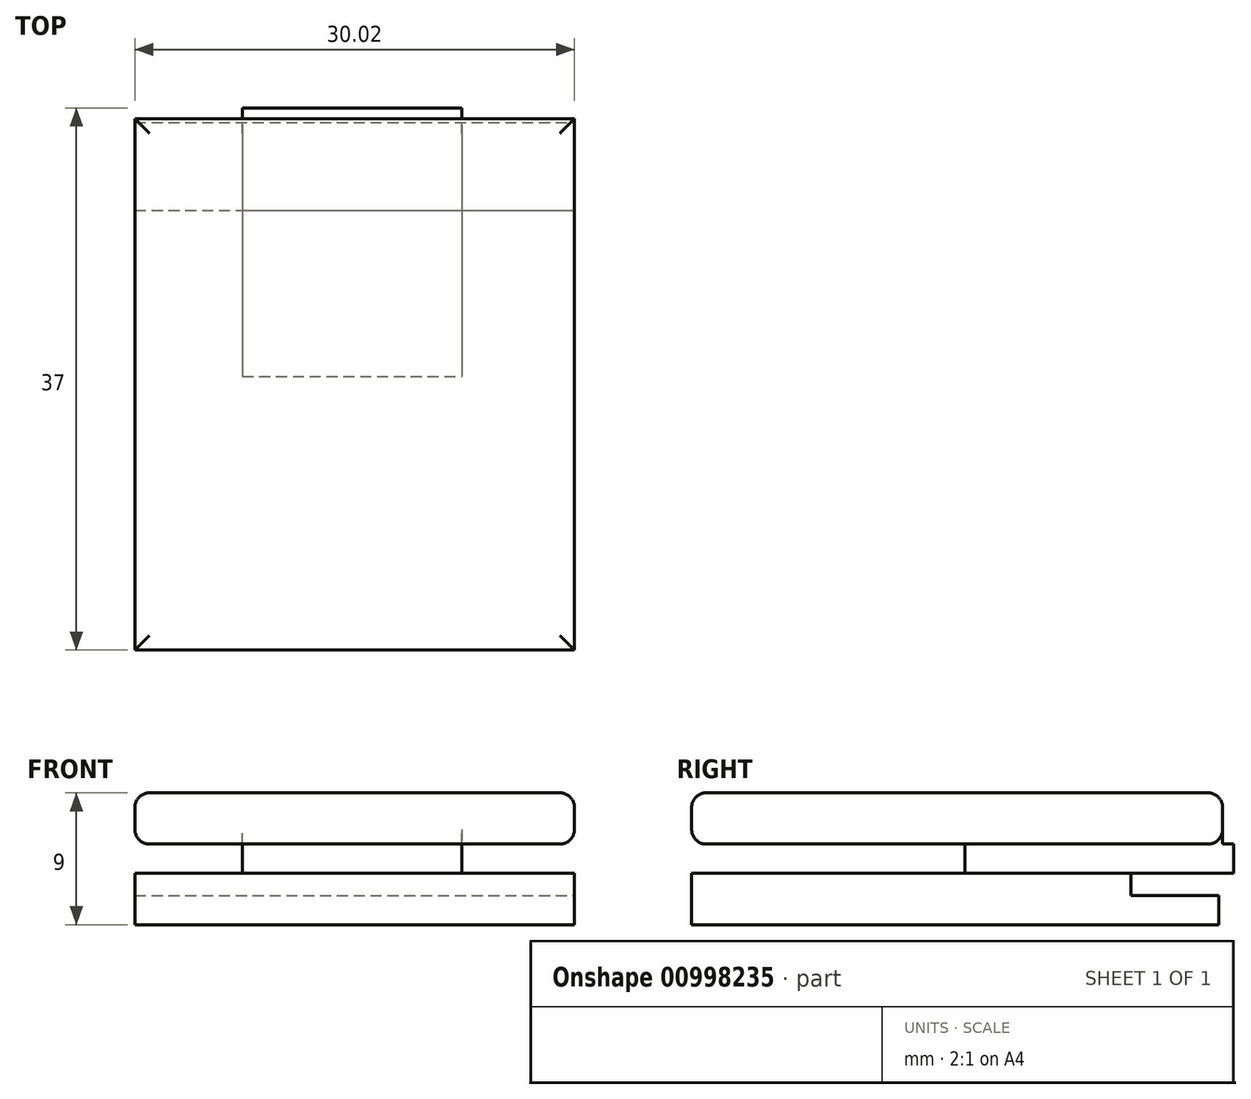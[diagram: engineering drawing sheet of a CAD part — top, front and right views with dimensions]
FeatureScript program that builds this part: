
annotation { "Feature Type Name" : "Feature", "Feature Type Description" : "" }
export const myFeature = defineFeature(function(context is Context, id is Id, definition is map)
    precondition{}
    {
        {
            var Q0;
            Q0=qCreatedBy(makeId("Top.planeOp"),FACE);
            var sketch = newSketch(context, id + "F0", { "sketchPlane" : qUnion([Q0])});
            skLineSegment(sketch, "E0.bottom", {"start": v(0, 0) * mm, "end": v(30, 0) * mm});
            skLineSegment(sketch, "E0.top", {"start": v(0, 30) * mm, "end": v(30, 30) * mm});
            skLineSegment(sketch, "E0.left", {"start": v(0, 0) * mm, "end": v(0, 30) * mm});
            skLineSegment(sketch, "E0.right", {"start": v(30, 0) * mm, "end": v(30, 30) * mm});
            skSolve(sketch);
        }
        {
            var Q0;
            Q0=makeQuery(id+"F0.imprint","IMPRINT",FACE,{"disambiguationData":[TD([[makeQuery(id+"F0.imprint","IMPRINT",EDGE,{"derivedFrom":sQuery(id+"F0.wireOp",EDGE,"E0.bottom")}),1.0]])]});
            extrude(context, id + "F1", {"entities" : qUnion([Q0]), "depth" : 1.5 * mm, "offsetDistance" : 25 * mm});
        }
        {
            var Q0;
            Q0=makeQuery(id+"F1.opExtrude","CAP_FACE",FACE,{"disambiguationData":[OSD([sQuery(id+"F0.wireOp",EDGE,"E0.bottom"),sQuery(id+"F0.wireOp",EDGE,"E0.top"),sQuery(id+"F0.wireOp",EDGE,"E0.left"),sQuery(id+"F0.wireOp",EDGE,"E0.right")])],"isStart":false});
            var sketch = newSketch(context, id + "F2", { "sketchPlane" : qUnion([Q0])});
            skLineSegment(sketch, "E1.bottom", {"start": v(7.34, 37) * mm, "end": v(22.34, 37) * mm});
            skLineSegment(sketch, "E1.top", {"start": v(7.34, 18.66) * mm, "end": v(22.34, 18.66) * mm});
            skLineSegment(sketch, "E1.left", {"start": v(7.34, 37) * mm, "end": v(7.34, 18.66) * mm});
            skLineSegment(sketch, "E1.right", {"start": v(22.34, 37) * mm, "end": v(22.34, 18.66) * mm});
            skSolve(sketch);
        }
        {
            var Q0;
            Q0 = qSketchRegion(id + "F2", true);
            extrude(context, id + "F3", {"entities" : qUnion([Q0]), "operationType" : NewBodyOperationType.ADD, "depth" : 2 * mm, "offsetDistance" : 25 * mm});
        }
        {
            var Q0;
            Q0=makeQuery(id+"F1.opExtrude","CAP_FACE",FACE,{"disambiguationData":[OSD([sQuery(id+"F0.wireOp",EDGE,"E0.bottom"),sQuery(id+"F0.wireOp",EDGE,"E0.top"),sQuery(id+"F0.wireOp",EDGE,"E0.left"),sQuery(id+"F0.wireOp",EDGE,"E0.right")])],"isStart":true});
            var sketch = newSketch(context, id + "F4", { "sketchPlane" : qUnion([Q0])});
            skLineSegment(sketch, "E2.bottom", {"start": v(0, 0) * mm, "end": v(30, 0) * mm});
            skLineSegment(sketch, "E2.top", {"start": v(0, -36) * mm, "end": v(30, -36) * mm});
            skLineSegment(sketch, "E2.left", {"start": v(0, 0) * mm, "end": v(0, -36) * mm});
            skLineSegment(sketch, "E2.right", {"start": v(30, 0) * mm, "end": v(30, -36) * mm});
            skSolve(sketch);
        }
        {
            var Q0;
            Q0 = qSketchRegion(id + "F4", true);
            extrude(context, id + "F5", {"entities" : qUnion([Q0]), "operationType" : NewBodyOperationType.ADD, "depth" : 2 * mm, "offsetDistance" : 25 * mm});
        }
        {
            var Q0;
            Q0=makeQuery(id+"F3.opExtrude","CAP_FACE",FACE,{"disambiguationData":[OSD([sQuery(id+"F2.wireOp",EDGE,"E1.bottom"),sQuery(id+"F2.wireOp",EDGE,"E1.top"),sQuery(id+"F2.wireOp",EDGE,"E1.left"),sQuery(id+"F2.wireOp",EDGE,"E1.right")])],"isStart":false});
            var sketch = newSketch(context, id + "F6", { "sketchPlane" : qUnion([Q0])});
            skLineSegment(sketch, "E3.bottom", {"start": v(0, 0) * mm, "end": v(30.02, 0) * mm});
            skLineSegment(sketch, "E3.top", {"start": v(0, 36.26) * mm, "end": v(30.02, 36.26) * mm});
            skLineSegment(sketch, "E3.left", {"start": v(0, 0) * mm, "end": v(0, 36.26) * mm});
            skLineSegment(sketch, "E3.right", {"start": v(30.02, 0) * mm, "end": v(30.02, 36.26) * mm});
            skSolve(sketch);
        }
        {
            var Q0;
            Q0 = qSketchRegion(id + "F6", true);
            extrude(context, id + "F7", {"entities" : qUnion([Q0]), "operationType" : NewBodyOperationType.ADD, "depth" : 3.5 * mm, "offsetDistance" : 25 * mm});
        }
        {
            var Q0;
            Q0=makeQuery(id+"F7.opExtrude","CAP_EDGE",EDGE,{"disambiguationData":[OSD([sQuery(id+"F6.wireOp",EDGE,"E3.left")])],"isStart":false});
            var Q1;
            Q1=makeQuery(id+"F7.opExtrude","CAP_EDGE",EDGE,{"disambiguationData":[OSD([sQuery(id+"F6.wireOp",EDGE,"E3.top")])],"isStart":false});
            var Q2;
            Q2=makeQuery(id+"F7.opExtrude","CAP_EDGE",EDGE,{"disambiguationData":[OSD([sQuery(id+"F6.wireOp",EDGE,"E3.right")])],"isStart":false});
            var Q3;
            Q3=makeQuery(id+"F7.opExtrude","CAP_EDGE",EDGE,{"disambiguationData":[OSD([sQuery(id+"F6.wireOp",EDGE,"E3.bottom")])],"isStart":false});
            var Q4;
            {var subQ0=sQuery(id+"F6.wireOp",EDGE,"E3.top");Q4=makeQuery(id+"F7.boolean.opBoolean","SPLIT",EDGE,{"disambiguationData":[topologyDisambiguationEdgeConnected([makeQuery(id+"F3.opExtrude","CAP_FACE",FACE,{"disambiguationData":[OSD([sQuery(id+"F2.wireOp",EDGE,"E1.bottom"),sQuery(id+"F2.wireOp",EDGE,"E1.top"),sQuery(id+"F2.wireOp",EDGE,"E1.left"),sQuery(id+"F2.wireOp",EDGE,"E1.right")])],"isStart":false}),makeQuery(id+"F7.opExtrude","SWEPT_FACE",FACE,{"disambiguationData":[OSD([subQ0])]})])],"derivedFrom":makeQuery(id+"F7.opExtrude","CAP_EDGE",EDGE,{"disambiguationData":[OSD([subQ0])],"isStart":true})});}
            var Q5;
            Q5=makeQuery(id+"F7.opExtrude","CAP_EDGE",EDGE,{"disambiguationData":[OSD([sQuery(id+"F6.wireOp",EDGE,"E3.right")])],"isStart":true});
            var Q6;
            Q6=makeQuery(id+"F7.opExtrude","CAP_EDGE",EDGE,{"disambiguationData":[OSD([sQuery(id+"F6.wireOp",EDGE,"E3.bottom")])],"isStart":true});
            var Q7;
            Q7=makeQuery(id+"F7.opExtrude","CAP_EDGE",EDGE,{"disambiguationData":[OSD([sQuery(id+"F6.wireOp",EDGE,"E3.left")])],"isStart":true});
            fillet(context, id + "F8", {"entities" : qUnion([Q0, Q1, Q2, Q3, Q4, Q5, Q6, Q7]), "radius" : 1 * mm, "tangentPropagation" : true, "allowEdgeOverflow" : false});
        }
    });
